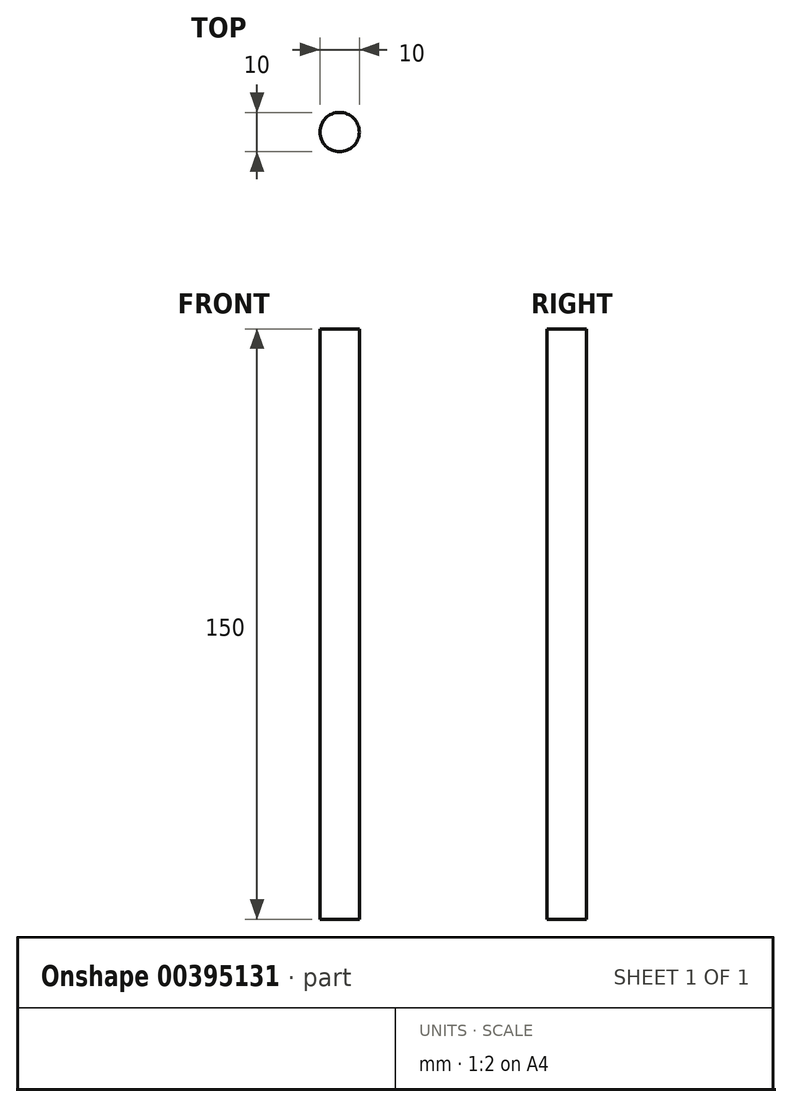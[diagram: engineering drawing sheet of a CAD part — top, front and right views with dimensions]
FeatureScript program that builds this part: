
annotation { "Feature Type Name" : "Feature", "Feature Type Description" : "" }
export const myFeature = defineFeature(function(context is Context, id is Id, definition is map)
    precondition{}
    {
        {
            var Q0;
            Q0=qCreatedBy(makeId("Top.planeOp"),FACE);
            var sketch = newSketch(context, id + "F0", { "sketchPlane" : qUnion([Q0])});
            skCircle(sketch, "E0", {"center": v(0, 0) * mm, "radius": 5 * mm});
            skSolve(sketch);
        }
        {
            var Q0;
            Q0 = qSketchRegion(id + "F0", true);
            extrude(context, id + "F1", {"entities" : qUnion([Q0]), "endBound" : BoundingType.SYMMETRIC, "offsetDistance" : 25 * mm, "depth" : 150 * mm});
        }
    });
